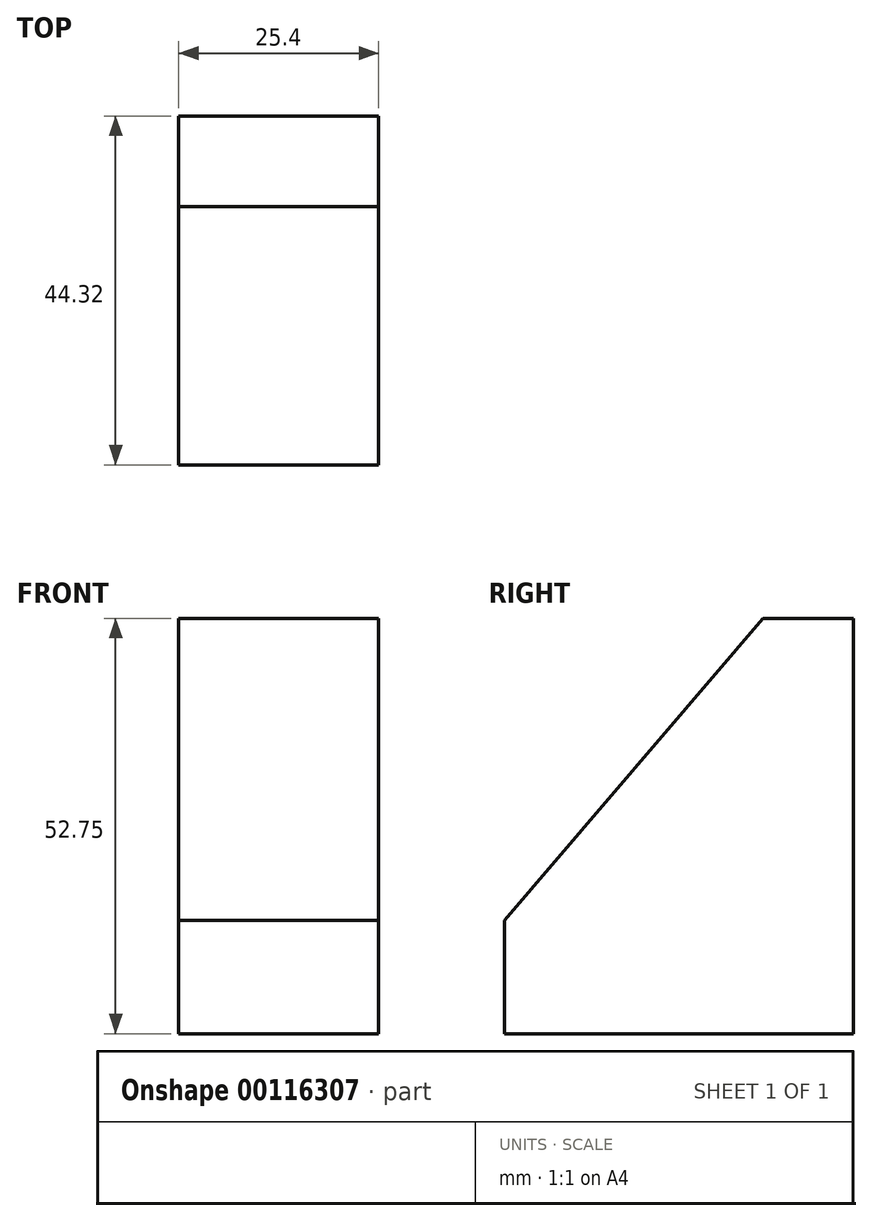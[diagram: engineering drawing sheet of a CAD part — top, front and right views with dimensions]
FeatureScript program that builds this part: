
annotation { "Feature Type Name" : "Feature", "Feature Type Description" : "" }
export const myFeature = defineFeature(function(context is Context, id is Id, definition is map)
    precondition{}
    {
        {
            var Q0;
            Q0=qCreatedBy(makeId("Right.planeOp"),FACE);
            var sketch = newSketch(context, id + "F0", { "sketchPlane" : qUnion([Q0])});
            skLineSegment(sketch, "E0", {"start": v(-23.5, -25.93) * mm, "end": v(-23.5, -11.52) * mm});
            skLineSegment(sketch, "E1", {"start": v(-23.5, -11.52) * mm, "end": v(9.3, 26.82) * mm});
            skLineSegment(sketch, "E2", {"start": v(9.3, 26.82) * mm, "end": v(20.83, 26.82) * mm});
            skLineSegment(sketch, "E3", {"start": v(20.83, 26.82) * mm, "end": v(20.83, -25.93) * mm});
            skLineSegment(sketch, "E4", {"start": v(20.83, -25.93) * mm, "end": v(-23.5, -25.93) * mm});
            skSolve(sketch);
        }
        {
            var Q0;
            Q0 = qSketchRegion(id + "F0", true);
            extrude(context, id + "F1", {"entities" : qUnion([Q0]), "depth" : 25.4 * mm});
        }
    });
